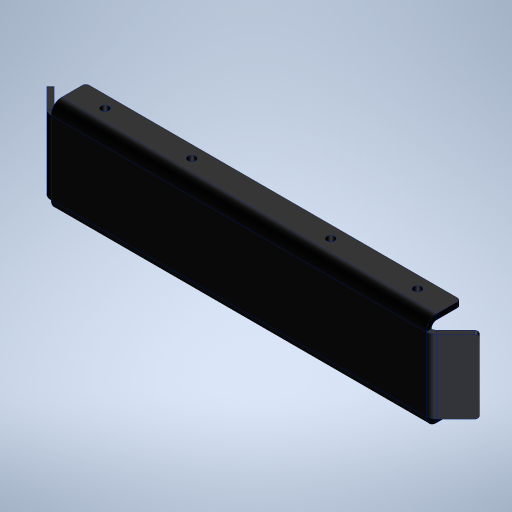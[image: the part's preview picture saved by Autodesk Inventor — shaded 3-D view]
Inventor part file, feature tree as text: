
AUTODESK INVENTOR PART (.ipt)
format: ipt  version: 2024 (Build 280153000, 153)  size: 327,680 bytes
history: native  units: mm
features: other x8, sketch x4, extrude x2, fillet x1
ambient origin geometry x8: Origin, YZ Plane, XZ Plane, XY Plane, X Axis, Y Axis, Z Axis, Center Point
bodies: Volumenkörper1 (feature_tree)
feature tree (15):
  extrude  "Extrusion1"  Depth=42.3mm
  other  "Lasche1"
  other  "Lasche2"
  extrude  "Extrusion2"  Depth=3.0mm
  fillet  "Rundung1"  Radius=3.0mm
  sketch  "Skizze1"  dims[d0=216.0mm d1=42.3mm]
  sketch  "Skizze2"  dims[d2=3.0mm d3=0.0mm d4=3.0mm d5=3.0mm]
  other  "Grobblech1"
  other  "Biegung1"
  other  "Ecke1"
  sketch  "Skizze3"  dims[d6=1.5mm]
  other  "Grobblech2"
  other  "Biegung2"
  other  "Ecke2"
  sketch  "Skizze4"  dims[d7=6.0mm d8=3.0mm d9=20.0mm d10=90.0deg d11=3.0mm d12=12.0mm d13=3.0mm d14=3.0mm d15=3.0mm d16=1.5mm d17=6.0mm d18=3.0mm d19=20.0mm d20=45.0deg d21=3.0mm d22=12.0mm d23=3.0mm d24=3.0mm d25=4.5mm d26=4.5mm d27=4.5mm d28=4.5mm d29=80.0mm d30=180.0mm d31=100.0mm d32=0.0mm d33=2.0mm]
